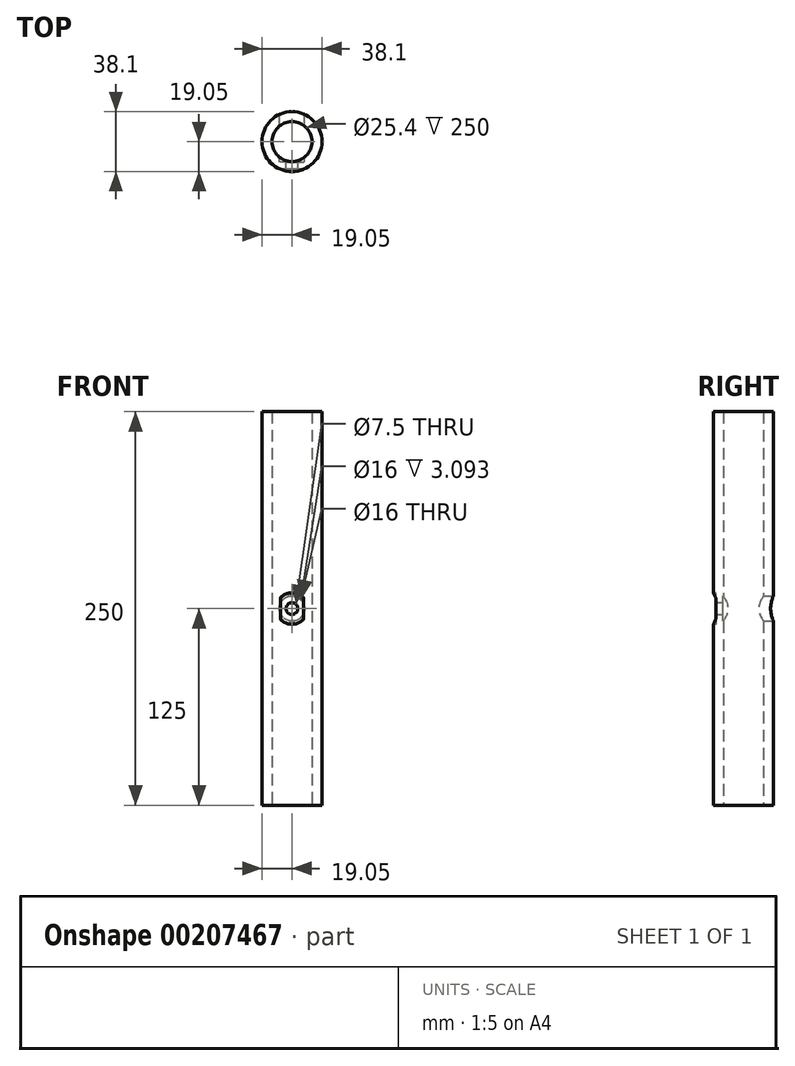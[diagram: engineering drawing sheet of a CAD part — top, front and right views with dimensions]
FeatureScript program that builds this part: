
annotation { "Feature Type Name" : "Feature", "Feature Type Description" : "" }
export const myFeature = defineFeature(function(context is Context, id is Id, definition is map)
    precondition{}
    {
        {
            var Q0;
            Q0=qCreatedBy(makeId("Top.planeOp"),FACE);
            var sketch = newSketch(context, id + "F0", { "sketchPlane" : qUnion([Q0])});
            skCircle(sketch, "E0", {"center": v(0, 0) * mm, "radius": 12.7 * mm});
            skCircle(sketch, "E1", {"center": v(0, 0) * mm, "radius": 19.05 * mm});
            skSolve(sketch);
        }
        {
            var Q0;
            Q0 = qSketchRegion(id + "F0", true);
            extrude(context, id + "F1", {"entities" : qUnion([Q0]), "depth" : 250 * mm});
        }
        {
            var Q0;
            Q0=qCreatedBy(makeId("Front.planeOp"),FACE);
            var sketch = newSketch(context, id + "F2", { "sketchPlane" : qUnion([Q0])});
            skCircle(sketch, "E2", {"center": v(0, 125) * mm, "radius": 3.75 * mm});
            skSolve(sketch);
        }
        {
            var Q0;
            Q0 = qSketchRegion(id + "F2", true);
            extrude(context, id + "F3", {"entities" : qUnion([Q0]), "operationType" : NewBodyOperationType.REMOVE, "endBound" : BoundingType.THROUGH_ALL, "oppositeDirection" : true, "depth" : 25 * mm});
        }
        {
            var Q0;
            Q0 = qSketchRegion(id + "F2", true);
            extrude(context, id + "F4", {"entities" : qUnion([Q0]), "operationType" : NewBodyOperationType.REMOVE, "endBound" : BoundingType.THROUGH_ALL, "depth" : 25 * mm});
        }
        {
            var Q0;
            Q0=qCreatedBy(makeId("Front.planeOp"),FACE);
            cPlane(context, id + "F5", {"entities" : qUnion([Q0]), "cplaneType" : CPlaneType.OFFSET, "offset" : 19.05 * mm, "oppositeDirection" : true, "width" : 150 * mm, "height" : 150 * mm});
        }
        {
            var Q0;
            Q0=qCreatedBy(id+"F5.planeOp",FACE);
            var sketch = newSketch(context, id + "F6", { "sketchPlane" : qUnion([Q0])});
            skCircle(sketch, "E3", {"center": v(0, 125) * mm, "radius": 8 * mm});
            skSolve(sketch);
        }
        {
            var Q0;
            Q0 = qSketchRegion(id + "F6", true);
            extrude(context, id + "F7", {"entities" : qUnion([Q0]), "operationType" : NewBodyOperationType.REMOVE, "depth" : 32 * mm});
        }
        {
            var Q0;
            Q0=qCreatedBy(makeId("Front.planeOp"),FACE);
            cPlane(context, id + "F8", {"entities" : qUnion([Q0]), "cplaneType" : CPlaneType.OFFSET, "offset" : 19.05 * mm, "width" : 150 * mm, "height" : 150 * mm});
        }
        {
            var Q0;
            Q0=qCreatedBy(id+"F8.planeOp",FACE);
            var sketch = newSketch(context, id + "F9", { "sketchPlane" : qUnion([Q0])});
            skCircle(sketch, "E4", {"center": v(0, 125) * mm, "radius": 10 * mm});
            skSolve(sketch);
        }
        {
            var Q0;
            Q0 = qSketchRegion(id + "F9", true);
            extrude(context, id + "F10", {"entities" : qUnion([Q0]), "operationType" : NewBodyOperationType.REMOVE, "oppositeDirection" : true, "depth" : 1.5 * mm});
        }
    });
